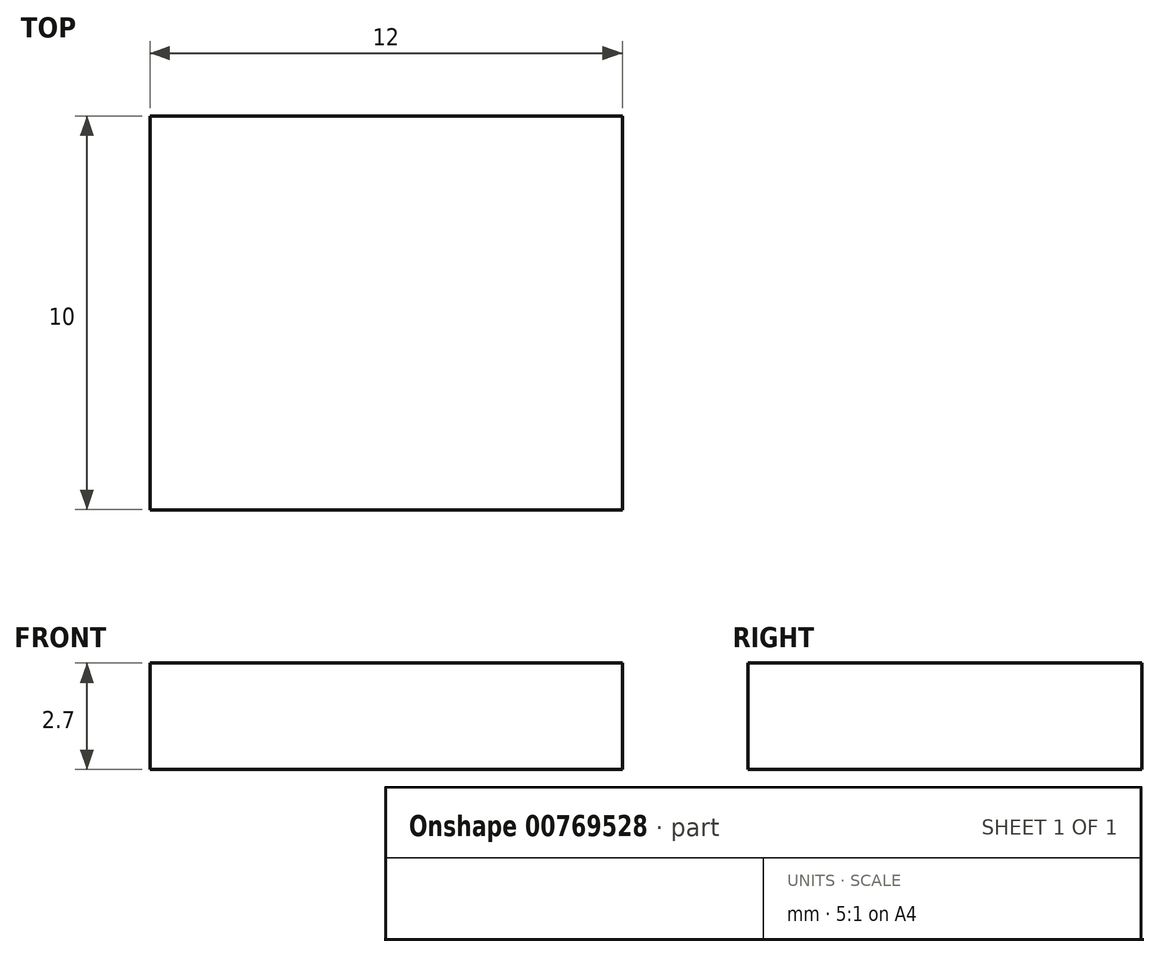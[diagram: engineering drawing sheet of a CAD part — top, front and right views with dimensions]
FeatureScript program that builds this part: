
annotation { "Feature Type Name" : "Feature", "Feature Type Description" : "" }
export const myFeature = defineFeature(function(context is Context, id is Id, definition is map)
    precondition{}
    {
        {
            var Q0;
            Q0=qCreatedBy(makeId("Top.planeOp"),FACE);
            var sketch = newSketch(context, id + "F0", { "sketchPlane" : qUnion([Q0])});
            skLineSegment(sketch, "E0.bottom", {"start": v(-22.27, -14.17) * mm, "end": v(-10.27, -14.17) * mm});
            skLineSegment(sketch, "E0.top", {"start": v(-22.27, -24.17) * mm, "end": v(-10.27, -24.17) * mm});
            skLineSegment(sketch, "E0.left", {"start": v(-22.27, -14.17) * mm, "end": v(-22.27, -24.17) * mm});
            skLineSegment(sketch, "E0.right", {"start": v(-10.27, -14.17) * mm, "end": v(-10.27, -24.17) * mm});
            skLineSegment(sketch, "E1", {"start": v(-10.27, -14.17) * mm, "end": v(-10.27, -10.17) * mm});
            skLineSegment(sketch, "E2", {"start": v(-10.27, -10.17) * mm, "end": v(-15.27, -10.17) * mm});
            skLineSegment(sketch, "E3", {"start": v(-15.27, -10.17) * mm, "end": v(-15.27, -14.17) * mm});
            skSolve(sketch);
        }
        {
            var Q0;
            Q0=makeQuery(id+"F0.imprint","IMPRINT",FACE,{"disambiguationData":[TD([[makeQuery(id+"F0.imprint","IMPRINT",EDGE,{"derivedFrom":sQuery(id+"F0.wireOp",EDGE,"E0.top")}),1.0]])]});
            extrude(context, id + "F1", {"entities" : qUnion([Q0]), "depth" : 2.7 * mm, "offsetDistance" : 25 * mm});
        }
    });
